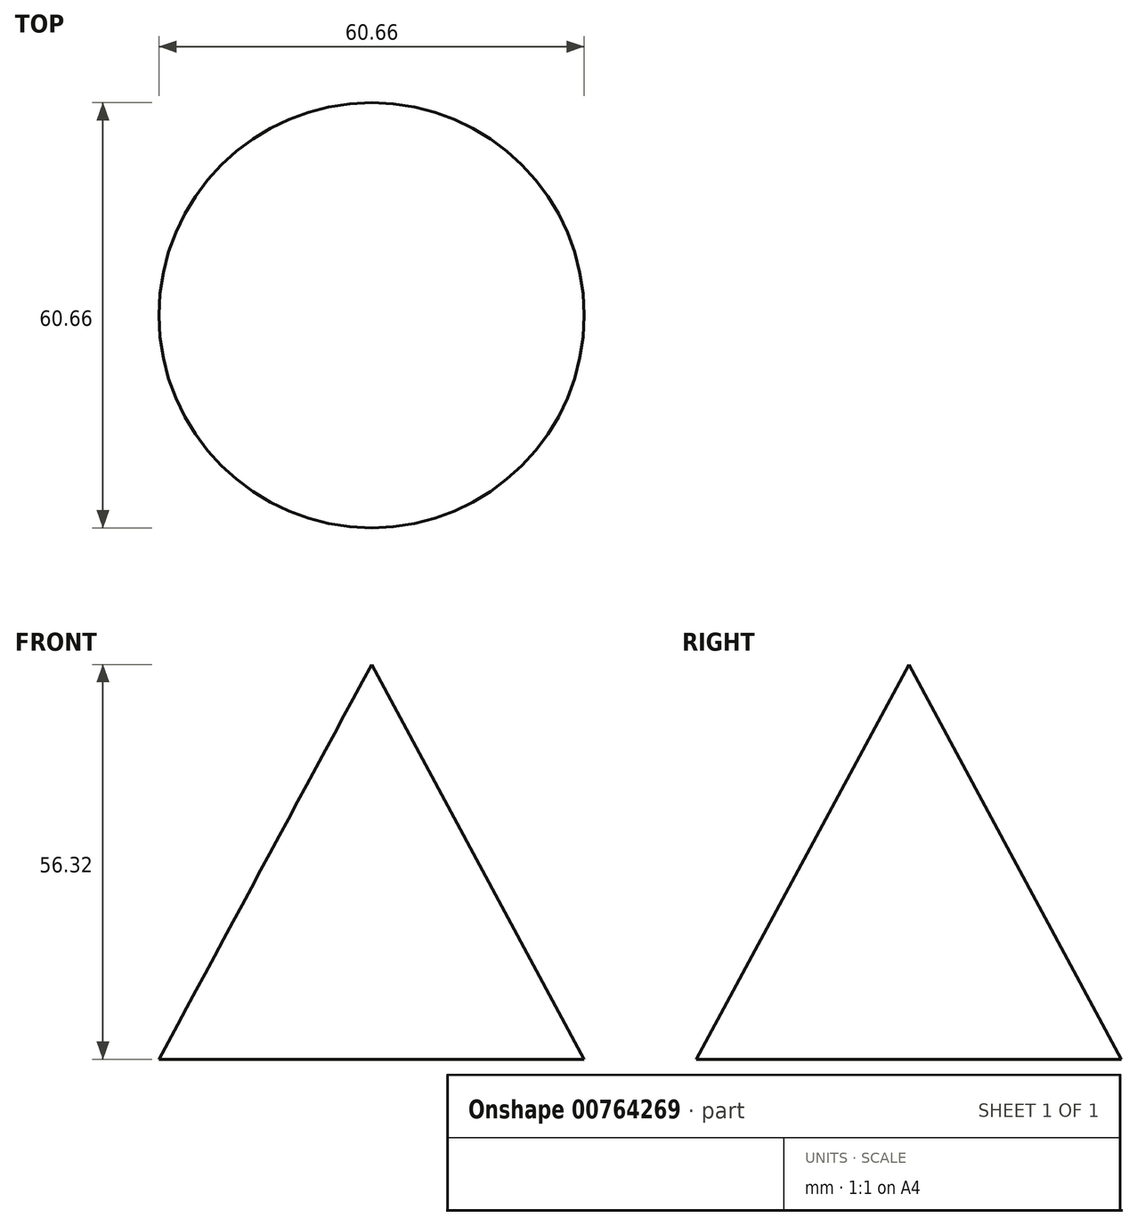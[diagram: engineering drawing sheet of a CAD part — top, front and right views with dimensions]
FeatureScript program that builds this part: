
annotation { "Feature Type Name" : "Feature", "Feature Type Description" : "" }
export const myFeature = defineFeature(function(context is Context, id is Id, definition is map)
    precondition{}
    {
        {
            var Q0;
            Q0=qCreatedBy(makeId("Front.planeOp"),FACE);
            var sketch = newSketch(context, id + "F0", { "sketchPlane" : qUnion([Q0])});
            skLineSegment(sketch, "E0", {"start": v(0, 56.32) * mm, "end": v(-30.33, 0) * mm});
            skLineSegment(sketch, "E1", {"start": v(-30.33, 0) * mm, "end": v(0, 0) * mm});
            skLineSegment(sketch, "E2", {"start": v(0, 0) * mm, "end": v(0, 56.32) * mm});
            skSolve(sketch);
        }
        {
            var Q0;
            Q0=makeQuery(id+"F0.imprint","IMPRINT",FACE,{"disambiguationData":[TD([[makeQuery(id+"F0.imprint","IMPRINT",EDGE,{"derivedFrom":sQuery(id+"F0.wireOp",EDGE,"E0")}),1.0]])]});
            var Q1;
            Q1=sQuery(id+"F0.wireOp",EDGE,"E2");
            revolve(context, id + "F1", {"surfaceOperationType" : NewSurfaceOperationType.NEW, "entities" : qUnion([Q0]), "axis" : qUnion([Q1]), "revolveType" : RevolveType.FULL});
        }
        {
            var Q0;
            Q0=makeQuery(id+"F1.opRevolve","SWEPT_FACE",FACE,{"disambiguationData":[OSD([sQuery(id+"F0.wireOp",EDGE,"E1")])]});
            var sketch = newSketch(context, id + "F2", { "sketchPlane" : qUnion([Q0])});
            skLineSegment(sketch, "E3", {"start": v(-16.32, -76.42) * mm, "end": v(-16.32, 75.3) * mm});
            skSolve(sketch);
        }
        {
            var Q0;
            Q0=qCreatedBy(makeId("Top.planeOp"),FACE);
            var sketch = newSketch(context, id + "F3", { "sketchPlane" : qUnion([Q0])});
            skLineSegment(sketch, "E4", {"start": v(-15.24, 45.9) * mm, "end": v(-15.24, -50.23) * mm});
            skSolve(sketch);
        }
        {
            var Q0;
            Q0=sQuery(id+"F3.wireOp",EDGE,"E4");
            extrude(context, id + "F4", {"bodyType" : ToolBodyType.SURFACE, "surfaceEntities" : qUnion([Q0]), "endBound" : BoundingType.SYMMETRIC, "depth" : 137.16 * mm, "offsetDistance" : 25.4 * mm});
        }
        {
            var Q0;
            Q0=qCreatedBy(makeId("Right.planeOp"),FACE);
            var sketch = newSketch(context, id + "F5", { "sketchPlane" : qUnion([Q0])});
            skLineSegment(sketch, "E5", {"start": v(-64.18, 43.54) * mm, "end": v(68.7, 43.54) * mm});
            skSolve(sketch);
        }
        {
            var Q0;
            Q0=sQuery(id+"F5.wireOp",EDGE,"E5");
            extrude(context, id + "F6", {"bodyType" : ToolBodyType.SURFACE, "surfaceEntities" : qUnion([Q0]), "endBound" : BoundingType.SYMMETRIC, "depth" : 105.16 * mm, "offsetDistance" : 25.4 * mm});
        }
    });
